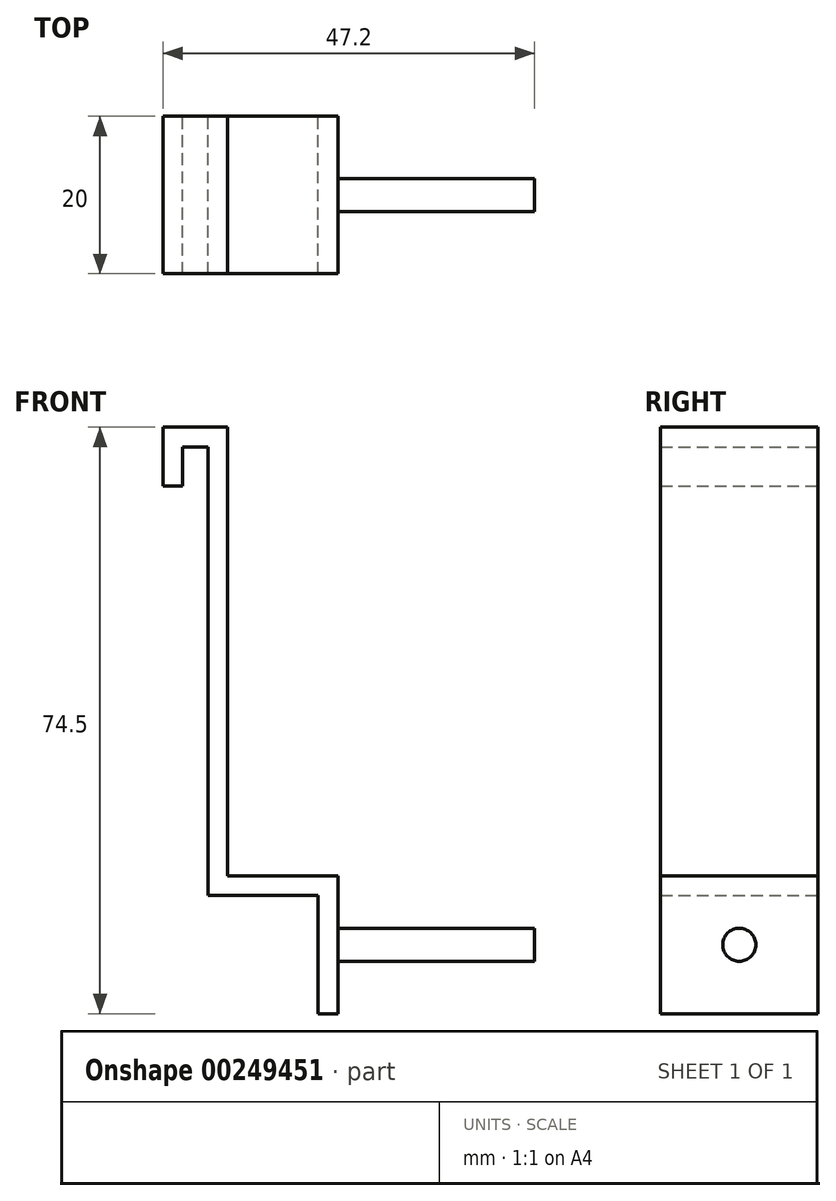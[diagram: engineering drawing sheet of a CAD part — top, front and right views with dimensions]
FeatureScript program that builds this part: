
annotation { "Feature Type Name" : "Feature", "Feature Type Description" : "" }
export const myFeature = defineFeature(function(context is Context, id is Id, definition is map)
    precondition{}
    {
        {
            var Q0;
            Q0=qCreatedBy(makeId("Front.planeOp"),FACE);
            var sketch = newSketch(context, id + "F0", { "sketchPlane" : qUnion([Q0])});
            skLineSegment(sketch, "E0", {"start": v(0, 0) * mm, "end": v(0, 7.5) * mm});
            skLineSegment(sketch, "E1", {"start": v(0, 0) * mm, "end": v(2.5, 0) * mm});
            skLineSegment(sketch, "E2", {"start": v(2.5, 0) * mm, "end": v(2.5, 5) * mm});
            skLineSegment(sketch, "E3", {"start": v(0, 7.5) * mm, "end": v(8.2, 7.5) * mm});
            skLineSegment(sketch, "E4", {"start": v(2.5, 5) * mm, "end": v(5.7, 5) * mm});
            skLineSegment(sketch, "E5", {"start": v(5.7, 5) * mm, "end": v(5.7, -52) * mm});
            skLineSegment(sketch, "E6", {"start": v(8.2, 7.5) * mm, "end": v(8.2, -49.5) * mm});
            skLineSegment(sketch, "E7", {"start": v(8.2, -49.5) * mm, "end": v(22.2, -49.5) * mm});
            skLineSegment(sketch, "E8", {"start": v(5.7, -52) * mm, "end": v(19.7, -52) * mm});
            skPoint(sketch, "E9.end.orphan", {"position": v(22.2, -52) * mm});
            skLineSegment(sketch, "E10", {"start": v(19.7, -52) * mm, "end": v(19.7, -67) * mm});
            skLineSegment(sketch, "E11", {"start": v(22.2, -49.5) * mm, "end": v(22.2, -67) * mm});
            skLineSegment(sketch, "E12", {"start": v(22.2, -67) * mm, "end": v(19.7, -67) * mm});
            skSolve(sketch);
        }
        {
            var Q0;
            Q0=makeQuery(id+"F0.imprint","IMPRINT",FACE,{"disambiguationData":[TD([[makeQuery(id+"F0.imprint","IMPRINT",EDGE,{"derivedFrom":sQuery(id+"F0.wireOp",EDGE,"E0")}),-1.0]])]});
            extrude(context, id + "F1", {"entities" : qUnion([Q0]), "depth" : 20 * mm});
        }
        {
            var Q0;
            Q0=makeQuery(id+"F1.opExtrude","SWEPT_FACE",FACE,{"disambiguationData":[OSD([sQuery(id+"F0.wireOp",EDGE,"E11")])]});
            var sketch = newSketch(context, id + "F2", { "sketchPlane" : qUnion([Q0])});
            skLineSegment(sketch, "E13", {"start": v(-20, -49.5) * mm, "end": v(0, -67) * mm, "construction": true});
            skLineSegment(sketch, "E14", {"start": v(0, -49.5) * mm, "end": v(-20, -67) * mm, "construction": true});
            skCircle(sketch, "E15", {"center": v(-10, -58.25) * mm, "radius": 2.1 * mm});
            skSolve(sketch);
        }
        {
            var Q0;
            Q0=makeQuery(id+"F2.imprint","IMPRINT",FACE,{"disambiguationData":[TD([[makeQuery(id+"F2.imprint","IMPRINT",EDGE,{"derivedFrom":sQuery(id+"F2.wireOp",EDGE,"E15")}),1.0]])]});
            extrude(context, id + "F3", {"entities" : qUnion([Q0]), "operationType" : NewBodyOperationType.ADD, "depth" : 25 * mm});
        }
    });
